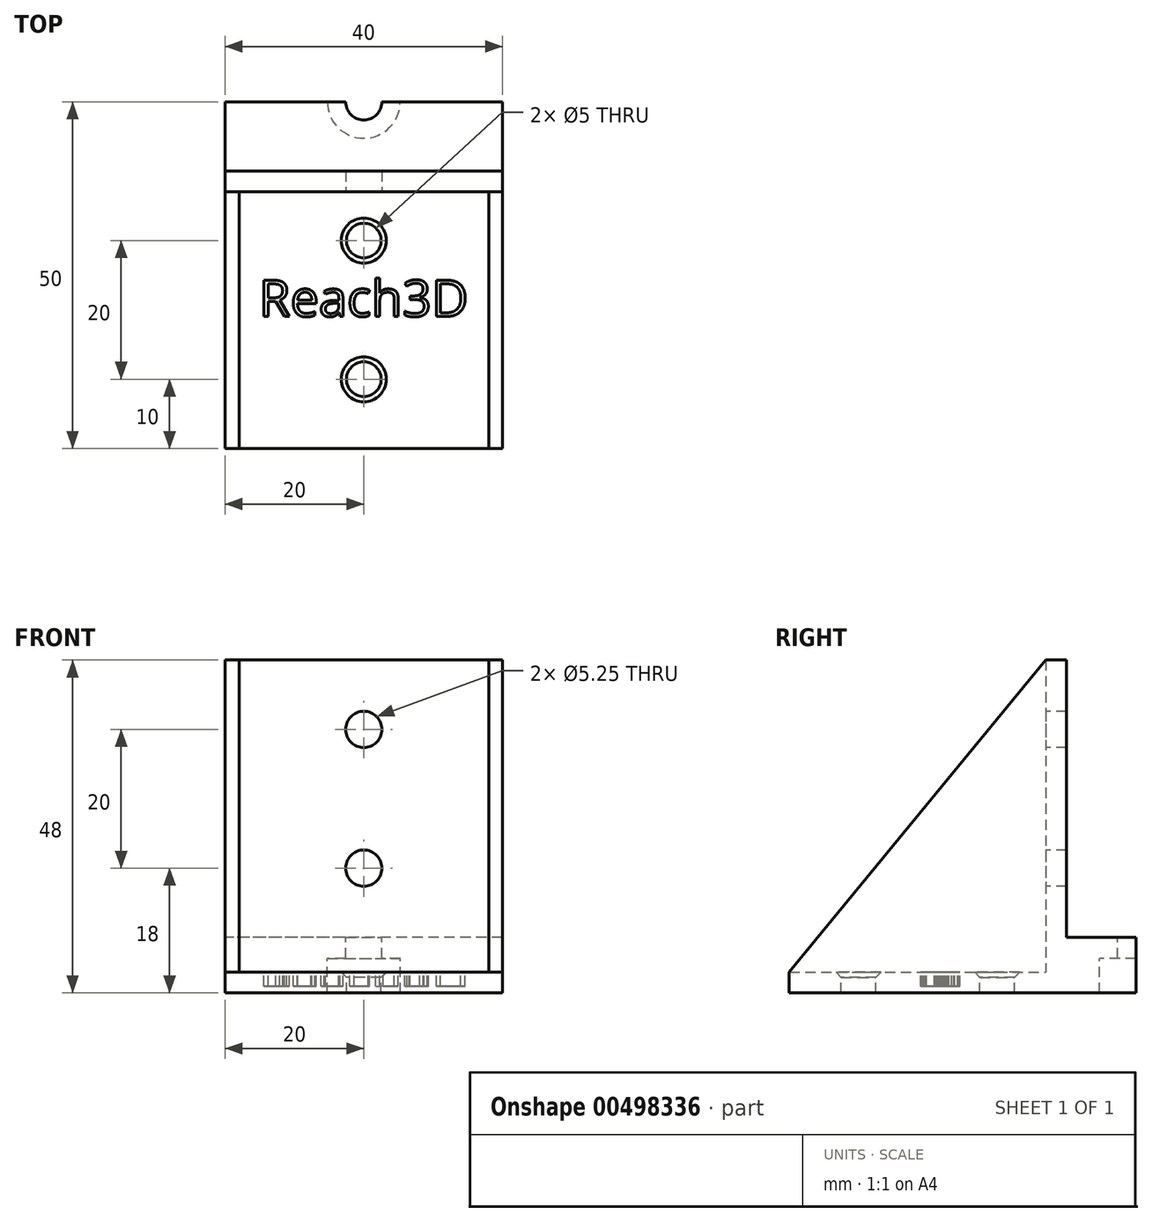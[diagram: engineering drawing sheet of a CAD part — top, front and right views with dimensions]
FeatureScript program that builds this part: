
annotation { "Feature Type Name" : "Feature", "Feature Type Description" : "" }
export const myFeature = defineFeature(function(context is Context, id is Id, definition is map)
    precondition{}
    {
        {
            var Q0;
            Q0=qCreatedBy(makeId("Right.planeOp"),FACE);
            var sketch = newSketch(context, id + "F0", { "sketchPlane" : qUnion([Q0])});
            skLineSegment(sketch, "E0.bottom", {"start": v(20, -24) * mm, "end": v(-20, -24) * mm});
            skLineSegment(sketch, "E0.top", {"start": v(20, 24) * mm, "end": v(-20, 24) * mm});
            skLineSegment(sketch, "E0.left", {"start": v(20, -24) * mm, "end": v(20, 24) * mm});
            skLineSegment(sketch, "E0.right", {"start": v(-20, -24) * mm, "end": v(-20, 24) * mm});
            skPoint(sketch, "E0.middle", {"position": v(0, 0) * mm});
            skLineSegment(sketch, "E1", {"start": v(17, 24) * mm, "end": v(17, -24) * mm});
            skLineSegment(sketch, "E2", {"start": v(-20, -21) * mm, "end": v(20, -21) * mm});
            skPoint(sketch, "E3", {"position": v(17, 24) * mm});
            skPoint(sketch, "E4", {"position": v(20, 24) * mm});
            skPoint(sketch, "E5", {"position": v(20, -21) * mm});
            skPoint(sketch, "E6", {"position": v(17, -24) * mm});
            skPoint(sketch, "E7", {"position": v(20, -24) * mm});
            skPoint(sketch, "E8", {"position": v(-20, -21) * mm});
            skPoint(sketch, "E9", {"position": v(-20, -24) * mm});
            skPoint(sketch, "E10", {"position": v(-20, 24) * mm});
            skLineSegment(sketch, "E11", {"start": v(17, 24) * mm, "end": v(-20, -21) * mm});
            skLineSegment(sketch, "E12.bottom", {"start": v(20, -24) * mm, "end": v(40, -24) * mm});
            skLineSegment(sketch, "E12.top", {"start": v(20, -16) * mm, "end": v(40, -16) * mm});
            skLineSegment(sketch, "E12.left", {"start": v(20, -24) * mm, "end": v(20, -16) * mm});
            skLineSegment(sketch, "E12.right", {"start": v(40, -24) * mm, "end": v(40, -16) * mm});
            skSolve(sketch);
        }
        {
            var Q0;
            {var subQ0=sQuery(id+"F0.wireOp",EDGE,"E0.left");var subQ1=sQuery(id+"F0.wireOp",EDGE,"E0.top");var subQ2=makeQuery(id+"F0.imprint","INTERSECT",VERTEX,{"derivedFrom":[subQ1,subQ0]});Q0=makeQuery(id+"F0.imprint","IMPRINT",FACE,{"disambiguationData":[TD([[makeQuery(id+"F0.imprint","IMPRINT",EDGE,{"disambiguationData":[TD([[subQ2,1.0]])],"derivedFrom":subQ0}),1.0]])]});}
            var Q1;
            {var subQ0=sQuery(id+"F0.wireOp",EDGE,"E11");Q1=makeQuery(id+"F0.imprint","IMPRINT",FACE,{"disambiguationData":[TD([[makeQuery(id+"F0.imprint","IMPRINT",EDGE,{"derivedFrom":subQ0}),1.0]])]});}
            var Q2;
            {var subQ0=sQuery(id+"F0.wireOp",EDGE,"E0.right");var subQ1=sQuery(id+"F0.wireOp",EDGE,"E0.bottom");var subQ2=makeQuery(id+"F0.imprint","INTERSECT",VERTEX,{"derivedFrom":[subQ1,subQ0]});Q2=makeQuery(id+"F0.imprint","IMPRINT",FACE,{"disambiguationData":[TD([[makeQuery(id+"F0.imprint","IMPRINT",EDGE,{"disambiguationData":[TD([[subQ2,1.0]])],"derivedFrom":subQ1}),-1.0]])]});}
            var Q3;
            {var subQ0=sQuery(id+"F0.wireOp",EDGE,"E0.left");var subQ1=sQuery(id+"F0.wireOp",EDGE,"E0.bottom");var subQ2=makeQuery(id+"F0.imprint","INTERSECT",VERTEX,{"derivedFrom":[subQ1,subQ0]});Q3=makeQuery(id+"F0.imprint","IMPRINT",FACE,{"disambiguationData":[TD([[makeQuery(id+"F0.imprint","IMPRINT",EDGE,{"disambiguationData":[TD([[subQ2,-1.0]])],"derivedFrom":subQ1}),-1.0]])]});}
            var Q4;
            {var subQ1=sQuery(id+"F0.wireOp",EDGE,"E0.bottom");var subQ3=sQuery(id+"F0.wireOp",EDGE,"E1");var subQ4=makeQuery(id+"F0.imprint","INTERSECT",VERTEX,{"derivedFrom":[subQ1,subQ3]});Q4=makeQuery(id+"F0.imprint","IMPRINT",FACE,{"disambiguationData":[TD([[makeQuery(id+"F0.imprint","IMPRINT",EDGE,{"disambiguationData":[TD([[subQ4,1.0]])],"derivedFrom":subQ3}),1.0]])]});}
            var Q5;
            {var subQ3=sQuery(id+"F0.wireOp",EDGE,"E12.bottom");Q5=makeQuery(id+"F0.imprint","IMPRINT",FACE,{"disambiguationData":[TD([[makeQuery(id+"F0.imprint","IMPRINT",EDGE,{"derivedFrom":subQ3}),1.0]])]});}
            extrude(context, id + "F1", {"entities" : qUnion([Q0, Q1, Q2, Q3, Q4, Q5]), "depth" : 20 * mm, "hasSecondDirection" : true, "secondDirectionOppositeDirection" : true, "secondDirectionDepth" : 20 * mm, "offsetDistance" : 25 * mm});
        }
        {
            var Q0;
            {var subQ0=sQuery(id+"F0.wireOp",EDGE,"E11");Q0=makeQuery(id+"F0.imprint","IMPRINT",FACE,{"disambiguationData":[TD([[makeQuery(id+"F0.imprint","IMPRINT",EDGE,{"derivedFrom":subQ0}),1.0]])]});}
            extrude(context, id + "F2", {"entities" : qUnion([Q0]), "operationType" : NewBodyOperationType.REMOVE, "depth" : 18 * mm, "hasSecondDirection" : true, "secondDirectionOppositeDirection" : true, "secondDirectionDepth" : 18 * mm, "offsetDistance" : 25 * mm});
        }
        {
            var Q0;
            Q0=qCreatedBy(makeId("Front.planeOp"),FACE);
            var sketch = newSketch(context, id + "F3", { "sketchPlane" : qUnion([Q0])});
            skLineSegment(sketch, "E13", {"start": v(0, 0) * mm, "end": v(0, 14) * mm});
            skLineSegment(sketch, "E14", {"start": v(0, 0) * mm, "end": v(0, -6) * mm});
            skCircle(sketch, "E15", {"center": v(0, 14) * mm, "radius": 2.62 * mm});
            skCircle(sketch, "E16", {"center": v(0, -6) * mm, "radius": 2.62 * mm});
            skSolve(sketch);
        }
        {
            var Q0;
            Q0=makeQuery(id+"F3.imprint","IMPRINT",FACE,{"disambiguationData":[TD([[makeQuery(id+"F3.imprint","IMPRINT",EDGE,{"derivedFrom":sQuery(id+"F3.wireOp",EDGE,"E15")}),1.0]])]});
            var Q1;
            Q1=makeQuery(id+"F3.imprint","IMPRINT",FACE,{"disambiguationData":[TD([[makeQuery(id+"F3.imprint","IMPRINT",EDGE,{"derivedFrom":sQuery(id+"F3.wireOp",EDGE,"E16")}),1.0]])]});
            var Q2;
            Q2=sQuery(id+"F3.wireOp",EDGE,"E15");
            var Q3;
            Q3=sQuery(id+"F3.wireOp",EDGE,"E16");
            extrude(context, id + "F4", {"entities" : qUnion([Q0, Q1]), "operationType" : NewBodyOperationType.REMOVE, "surfaceEntities" : qUnion([Q2, Q3]), "oppositeDirection" : true, "depth" : 25.1 * mm});
        }
        {
            var Q0;
            Q0=qCreatedBy(makeId("Top.planeOp"),FACE);
            var sketch = newSketch(context, id + "F5", { "sketchPlane" : qUnion([Q0])});
            skLineSegment(sketch, "E17", {"start": v(0, 0) * mm, "end": v(0, 10) * mm});
            skLineSegment(sketch, "E18", {"start": v(0, 0) * mm, "end": v(0, -10) * mm});
            skCircle(sketch, "E19", {"center": v(0, 10) * mm, "radius": 2.5 * mm});
            skCircle(sketch, "E20", {"center": v(0, -10) * mm, "radius": 2.5 * mm});
            skText(sketch, "E21", { "text": "Reach3D", "fontName": "OpenSans-Regular.ttf"});
            skLineSegment(sketch, "E22", {"start": v(0, 20) * mm, "end": v(0, 40) * mm, "construction": true});
            skPoint(sketch, "E23", {"position": v(0, 30) * mm});
            skCircle(sketch, "E24", {"center": v(0, 30) * mm, "radius": 2.62 * mm});
            skCircle(sketch, "E25", {"center": v(0, 30) * mm, "radius": 5.25 * mm});
            skLineSegment(sketch, "E26", {"start": v(0, 30) * mm, "end": v(-22.27, 30) * mm});
            skLineSegment(sketch, "E27", {"start": v(-22.27, 30) * mm, "end": v(-22.27, 41.23) * mm});
            skLineSegment(sketch, "E28", {"start": v(-22.27, 41.23) * mm, "end": v(21.14, 41.23) * mm});
            skLineSegment(sketch, "E29", {"start": v(21.14, 41.23) * mm, "end": v(21.14, 30) * mm});
            skLineSegment(sketch, "E30", {"start": v(21.14, 30) * mm, "end": v(0, 30) * mm});
            const initialGuessF5  = {"E21": [-0.01512, -0.00095, 1, 0, 0.00527]};
            skSetInitialGuess(sketch, initialGuessF5);
            skSolve(sketch);
        }
        {
            var Q0;
            Q0=makeQuery(id+"F5.imprint","IMPRINT",FACE,{"disambiguationData":[TD([[makeQuery(id+"F5.imprint","IMPRINT",EDGE,{"derivedFrom":sQuery(id+"F5.wireOp",EDGE,"E19")}),1.0]])]});
            var Q1;
            Q1=makeQuery(id+"F5.imprint","IMPRINT",FACE,{"disambiguationData":[TD([[makeQuery(id+"F5.imprint","IMPRINT",EDGE,{"derivedFrom":sQuery(id+"F5.wireOp",EDGE,"E20")}),1.0]])]});
            extrude(context, id + "F6", {"entities" : qUnion([Q0, Q1]), "operationType" : NewBodyOperationType.REMOVE, "oppositeDirection" : true, "depth" : 25 * mm});
        }
        {
            var Q0;
            Q0=makeQuery(id+"F5.imprint","IMPRINT",FACE,{"disambiguationData":[TD([[makeQuery(id+"F5.imprint","IMPRINT",EDGE,{"derivedFrom":sQuery(id+"F5.wireOp",EDGE,"E21.sketch_text.stroke-97")}),-1.0]])]});
            var Q1;
            Q1=makeQuery(id+"F5.imprint","IMPRINT",FACE,{"disambiguationData":[TD([[makeQuery(id+"F5.imprint","IMPRINT",EDGE,{"derivedFrom":sQuery(id+"F5.wireOp",EDGE,"E21.sketch_text.stroke-125")}),-1.0]])]});
            var Q2;
            Q2=makeQuery(id+"F5.imprint","IMPRINT",FACE,{"disambiguationData":[TD([[makeQuery(id+"F5.imprint","IMPRINT",EDGE,{"derivedFrom":sQuery(id+"F5.wireOp",EDGE,"E21.sketch_text.stroke-79")}),-1.0]])]});
            var Q3;
            {var subQ11=sQuery(id+"F5.wireOp",EDGE,"E21.sketch_text.stroke-64");Q3=makeQuery(id+"F5.imprint","IMPRINT",FACE,{"disambiguationData":[TD([[makeQuery(id+"F5.imprint","IMPRINT",EDGE,{"derivedFrom":subQ11}),-1.0]])]});}
            var Q4;
            {var subQ0=sQuery(id+"F5.wireOp",EDGE,"E21.sketch_text.stroke-69");Q4=makeQuery(id+"F5.imprint","IMPRINT",FACE,{"disambiguationData":[TD([[makeQuery(id+"F5.imprint","IMPRINT",EDGE,{"derivedFrom":subQ0}),-1.0]])]});}
            var Q5;
            {var subQ5=sQuery(id+"F5.wireOp",EDGE,"E21.sketch_text.stroke-77");Q5=makeQuery(id+"F5.imprint","IMPRINT",FACE,{"disambiguationData":[TD([[makeQuery(id+"F5.imprint","IMPRINT",EDGE,{"derivedFrom":subQ5}),-1.0]])]});}
            var Q6;
            Q6=makeQuery(id+"F5.imprint","IMPRINT",FACE,{"disambiguationData":[TD([[makeQuery(id+"F5.imprint","IMPRINT",EDGE,{"derivedFrom":sQuery(id+"F5.wireOp",EDGE,"E21.sketch_text.stroke-37")}),-1.0]])]});
            var Q7;
            Q7=makeQuery(id+"F5.imprint","IMPRINT",FACE,{"disambiguationData":[TD([[makeQuery(id+"F5.imprint","IMPRINT",EDGE,{"derivedFrom":sQuery(id+"F5.wireOp",EDGE,"E21.sketch_text.stroke-18")}),-1.0]])]});
            var Q8;
            Q8=makeQuery(id+"F5.imprint","IMPRINT",FACE,{"disambiguationData":[TD([[makeQuery(id+"F5.imprint","IMPRINT",EDGE,{"derivedFrom":sQuery(id+"F5.wireOp",EDGE,"E21.sketch_text.stroke-0")}),-1.0]])]});
            extrude(context, id + "F7", {"entities" : qUnion([Q0, Q1, Q2, Q3, Q4, Q5, Q6, Q7, Q8]), "operationType" : NewBodyOperationType.REMOVE, "oppositeDirection" : true, "depth" : 23 * mm, "offsetDistance" : 25 * mm});
        }
        {
            var Q0;
            Q0=makeQuery(id+"F6.boolean.opBoolean","INTERSECT",EDGE,{"derivedFrom":[makeQuery(id+"F2.boolean.opBoolean","COPY",FACE,{"derivedFrom":makeQuery(id+"F2.opExtrude","SWEPT_FACE",FACE,{"disambiguationData":[OSD([sQuery(id+"F0.wireOp",EDGE,"E2")])]})}),makeQuery(id+"F6.opExtrude","SWEPT_FACE",FACE,{"disambiguationData":[OSD([sQuery(id+"F5.wireOp",EDGE,"E20")])]})]});
            var Q1;
            Q1=makeQuery(id+"F6.boolean.opBoolean","INTERSECT",EDGE,{"derivedFrom":[makeQuery(id+"F2.boolean.opBoolean","COPY",FACE,{"derivedFrom":makeQuery(id+"F2.opExtrude","SWEPT_FACE",FACE,{"disambiguationData":[OSD([sQuery(id+"F0.wireOp",EDGE,"E2")])]})}),makeQuery(id+"F6.opExtrude","SWEPT_FACE",FACE,{"disambiguationData":[OSD([sQuery(id+"F5.wireOp",EDGE,"E19")])]})]});
            chamfer(context, id + "F8", {"entities" : qUnion([Q0, Q1]), "width" : .75 * mm, "tangentPropagation" : true});
        }
        {
            var Q0;
            Q0=makeQuery(id+"F5.imprint","IMPRINT",FACE,{"disambiguationData":[TD([[makeQuery(id+"F5.imprint","IMPRINT",EDGE,{"derivedFrom":sQuery(id+"F5.wireOp",EDGE,"E24")}),-1.0]])]});
            var Q1;
            Q1=makeQuery(id+"F5.imprint","IMPRINT",FACE,{"disambiguationData":[TD([[makeQuery(id+"F5.imprint","IMPRINT",EDGE,{"derivedFrom":sQuery(id+"F5.wireOp",EDGE,"E24")}),1.0]])]});
            extrude(context, id + "F9", {"entities" : qUnion([Q0, Q1]), "operationType" : NewBodyOperationType.REMOVE, "oppositeDirection" : true, "depth" : 25 * mm, "offsetDistance" : 25 * mm});
        }
        {
            var Q0;
            Q0=makeQuery(id+"F5.imprint","IMPRINT",FACE,{"disambiguationData":[TD([[makeQuery(id+"F5.imprint","IMPRINT",EDGE,{"derivedFrom":sQuery(id+"F5.wireOp",EDGE,"E24")}),-1.0]])]});
            extrude(context, id + "F10", {"entities" : qUnion([Q0]), "operationType" : NewBodyOperationType.ADD, "oppositeDirection" : true, "depth" : 19 * mm, "offsetDistance" : 25 * mm});
        }
        {
            var Q0;
            Q0=makeQuery(id+"F5.imprint","IMPRINT",FACE,{"disambiguationData":[TD([[makeQuery(id+"F5.imprint","IMPRINT",EDGE,{"derivedFrom":sQuery(id+"F5.wireOp",EDGE,"E24")}),-1.0]])]});
            extrude(context, id + "F11", {"entities" : qUnion([Q0]), "operationType" : NewBodyOperationType.REMOVE, "oppositeDirection" : true, "depth" : 16 * mm, "offsetDistance" : 25 * mm});
        }
        {
            var Q0;
            {var subQ0=sQuery(id+"F5.wireOp",EDGE,"E27");Q0=makeQuery(id+"F5.imprint","IMPRINT",FACE,{"disambiguationData":[TD([[makeQuery(id+"F5.imprint","IMPRINT",EDGE,{"derivedFrom":subQ0}),-1.0]])]});}
            var Q1;
            {var subQ0=sQuery(id+"F5.wireOp",EDGE,"E26");var subQ1=sQuery(id+"F5.wireOp",EDGE,"E24");var subQ2=makeQuery(id+"F5.imprint","INTERSECT",VERTEX,{"derivedFrom":[subQ1,subQ0]});Q1=makeQuery(id+"F5.imprint","IMPRINT",FACE,{"disambiguationData":[TD([[makeQuery(id+"F5.imprint","IMPRINT",EDGE,{"disambiguationData":[TD([[subQ2,1.0]])],"derivedFrom":subQ1}),-1.0]])]});}
            extrude(context, id + "F12", {"entities" : qUnion([Q0, Q1]), "operationType" : NewBodyOperationType.REMOVE, "oppositeDirection" : true, "depth" : 25 * mm, "offsetDistance" : 25 * mm});
        }
    });
